# Revit family: Legrand_single_phase_circuit_separation_transformers
name_source: partatom
category: Installations électriques
revit_build: Autodesk Revit 2018 (Build: 20170223_1515(x64)
units: mm (PartAtom-declared; Revit-internal decimal feet)

## family parameters
Basée sur le plan de construction = Non
Conserver l'orientation des annotations = Non
Cote de connecteur circulaire = Utiliser le diamètre
Couper avec des vides une fois chargée = Non
Numéro OmniClass = 23.80.00.00
Partagée = Non
Point de calcul de pièce = Non
Titre OmniClass = Electric Power and Lighting
Toujours verticalement = Oui
Type d'élément = Normal

## types (11) — shared parameters
Characteristic = Class I - IP21 - IK08
Fabricant = Legrand
General Conditions of Use = https://export.legrand.com
Modèle = Circuit Separation Transformers
Primary voltage = 230V - 400V
Secondary voltage = 115V - 230V
URL = www.legrand.com

## per-type parameters (varying)
| type | 042517 | 042518 | 042555, 042556, 042557 | 042558 | 142559, 142560, 142561 | 142562, 142563 | Insulating | Primary Cable Section | Secondary cable section | Ucc (%) | dimension A | dimension B | dimension C | empty loss | fixing F | fixing G | fixing diameter | max totaly loss | power | weight |
| single phase transformer 042517 | Oui | Non | Non | Non | Non | Non | class B | 6mm² | 6 mm² | 1.6 | 250 mm  [stored 0.82021 ft] | 270 mm  [stored 0.885827 ft] | 253 mm  [stored 0.830052 ft] | 60 W | 240 mm  [stored 0.787402 ft] | 140 mm  [stored 0.459318 ft] | 7 mm  [stored 0.0229659 ft] | 92 W | 2 kVA | 25.00 kg |
| single phase transformer 042518 | Non | Oui | Non | Non | Non | Non | class B | 10mm² | 10 mm² | 2.2 | 320 mm  [stored 1.04987 ft] | 330 mm | 253 mm  [stored 0.830052 ft] | 89 W | 300 mm  [stored 0.984252 ft] | 111 mm | 9 mm  [stored 0.0295276 ft] | 136 W | 3 kVA | 33.00 kg |
| single phase transformer 042555 | Non | Non | Oui | Non | Non | Non | class H | 10mm² | 16 mm² | 1.8 | 340 mm  [stored 1.11549 ft] | 410 mm  [stored 1.34514 ft] | 320 mm  [stored 1.04987 ft] | 95 W | 320 mm  [stored 1.04987 ft] | 130 mm  [stored 0.426509 ft] | 9 mm  [stored 0.0295276 ft] | 197 W | 4 kVA | 49.00 kg |
| single phase transformer 042556 | Non | Non | Oui | Non | Non | Non | class H | 10mm² | 16 mm² | 1.7 | 340 mm  [stored 1.11549 ft] | 410 mm  [stored 1.34514 ft] | 320 mm  [stored 1.04987 ft] | 149 W | 320 mm  [stored 1.04987 ft] | 180 mm  [stored 0.590551 ft] | 9 mm  [stored 0.0295276 ft] | 279 W | 5 kVA | 65.00 kg |
| single phase transformer 042557 | Non | Non | Oui | Non | Non | Non | class H | 10mm² | 16 mm² | 1.9 | 340 mm  [stored 1.11549 ft] | 410 mm  [stored 1.34514 ft] | 320 mm  [stored 1.04987 ft] | 149 W | 320 mm  [stored 1.04987 ft] | 180 mm  [stored 0.590551 ft] | 9 mm  [stored 0.0295276 ft] | 326 W | 6 kVA | 74.00 kg |
| single phase transformer 042558 | Non | Non | Non | Oui | Non | Non | class H | 16mm² | 35 mm² | 1.8 | 390 mm  [stored 1.27953 ft] | 460 mm  [stored 1.50919 ft] | 380 mm  [stored 1.24672 ft] | 158 W | 370 mm  [stored 1.21391 ft] | 150 mm | 9 mm  [stored 0.0295276 ft] | 352 W | 8 kVA | 88.00 kg |
| single phase transformer 142559 | Non | Non | Non | Non | Oui | Non | class H | 16mm² | 35 mm² | 2.2 | 431 mm  [stored 1.41404 ft] | 650 mm  [stored 2.13255 ft] | 440 mm  [stored 1.44357 ft] | 135 W | 411 mm  [stored 1.34843 ft] | 146 mm  [stored 0.479003 ft] | 11 mm  [stored 0.0360892 ft] | 453 W | 10 kVA | 70.00 kg |
| single phase transformer 142560 | Non | Non | Non | Non | Oui | Non | class H | 16mm² | 35 mm² | 2.1 | 431 mm  [stored 1.41404 ft] | 650 mm  [stored 2.13255 ft] | 440 mm  [stored 1.44357 ft] | 135 W | 411 mm  [stored 1.34843 ft] | 146 mm  [stored 0.479003 ft] | 11 mm  [stored 0.0360892 ft] | 468 W | 13 kVA | 75.00 kg |
| single phase transformer 142561 | Non | Non | Non | Non | Oui | Non | class H | 35mm² | 70 mm² | 2.2 | 431 mm  [stored 1.41404 ft] | 650 mm  [stored 2.13255 ft] | 440 mm  [stored 1.44357 ft] | 135 W | 411 mm  [stored 1.34843 ft] | 146 mm  [stored 0.479003 ft] | 11 mm  [stored 0.0360892 ft] | 508 W | 16 kVA | 93.00 kg |
| single phase transformer 142562 | Non | Non | Non | Non | Non | Oui | class H | 35mm² | 70 mm² | 5.4 | 530 mm  [stored 1.73885 ft] | 560 mm  [stored 1.83727 ft] | 540 mm  [stored 1.77165 ft] | 148 W | 240 mm  [stored 0.787402 ft] | 510 mm  [stored 1.67323 ft] | 12 mm  [stored 0.0393701 ft] | 838 W | 20 kVA | 105.00 kg |
| single phase transformer 142563 | Non | Non | Non | Non | Non | Oui | class H | 35mm² | 70 mm² | 4.6 | 530 mm  [stored 1.73885 ft] | 560 mm  [stored 1.83727 ft] | 540 mm  [stored 1.77165 ft] | 189 W | 240 mm  [stored 0.787402 ft] | 510 mm  [stored 1.67323 ft] | 12 mm  [stored 0.0393701 ft] | 927 W | 25 kVA | 124.00 kg |

note: [stored X ft] marks values corroborated as IEEE doubles in the binary element streams (Revit-internal decimal feet)
